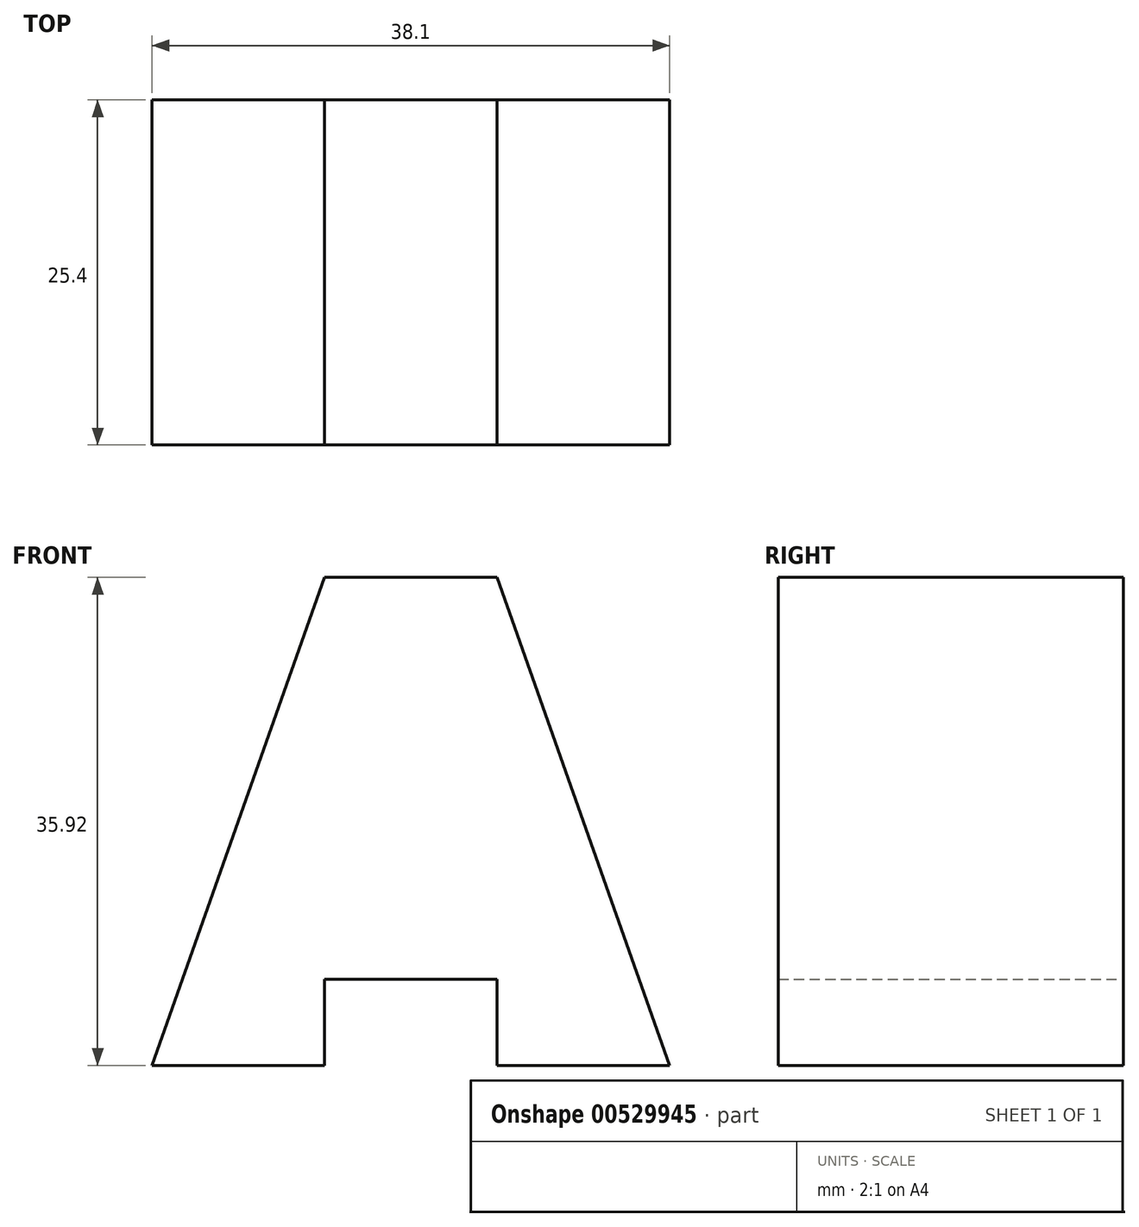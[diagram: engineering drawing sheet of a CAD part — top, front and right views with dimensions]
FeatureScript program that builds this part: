
annotation { "Feature Type Name" : "Feature", "Feature Type Description" : "" }
export const myFeature = defineFeature(function(context is Context, id is Id, definition is map)
    precondition{}
    {
        {
            var Q0;
            Q0=qCreatedBy(makeId("Front.planeOp"),FACE);
            var sketch = newSketch(context, id + "F0", { "sketchPlane" : qUnion([Q0])});
            skLineSegment(sketch, "E0", {"start": v(-62.73, 14.64) * mm, "end": v(-50.03, 14.64) * mm});
            skLineSegment(sketch, "E1", {"start": v(-50.03, 14.64) * mm, "end": v(-50.03, 20.99) * mm});
            skLineSegment(sketch, "E2", {"start": v(-50.03, 20.99) * mm, "end": v(-37.33, 20.99) * mm});
            skLineSegment(sketch, "E3", {"start": v(-37.33, 20.99) * mm, "end": v(-37.33, 14.64) * mm});
            skLineSegment(sketch, "E4", {"start": v(-37.33, 14.64) * mm, "end": v(-24.63, 14.64) * mm});
            skLineSegment(sketch, "E5", {"start": v(-24.63, 14.64) * mm, "end": v(-37.33, 50.56) * mm});
            skLineSegment(sketch, "E6", {"start": v(-62.73, 14.64) * mm, "end": v(-50.03, 50.56) * mm});
            skLineSegment(sketch, "E7", {"start": v(-50.03, 50.56) * mm, "end": v(-37.33, 50.56) * mm});
            skSolve(sketch);
        }
        {
            var Q0;
            Q0=makeQuery(id+"F0.imprint","IMPRINT",FACE,{"disambiguationData":[TD([[makeQuery(id+"F0.imprint","IMPRINT",EDGE,{"derivedFrom":sQuery(id+"F0.wireOp",EDGE,"E0")}),1.0]])]});
            extrude(context, id + "F1", {"entities" : qUnion([Q0]), "depth" : 25.4 * mm, "offsetDistance" : 25.4 * mm});
        }
    });
